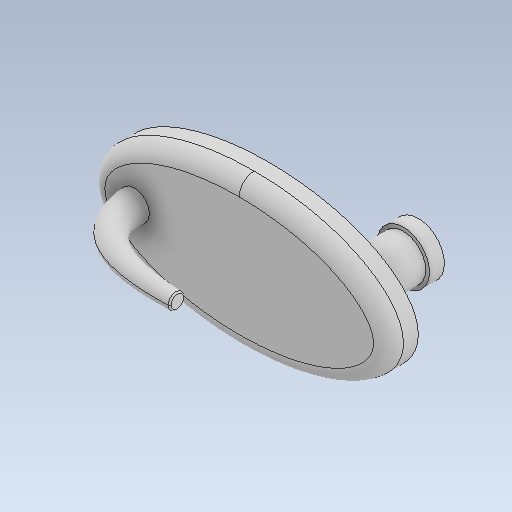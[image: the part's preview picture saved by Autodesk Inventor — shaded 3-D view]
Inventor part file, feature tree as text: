
AUTODESK INVENTOR PART (.ipt)
format: ipt  version: 2020.3 (Build 243373000, 373)  size: 243,200 bytes
history: native  units: in
note: dims shown in document units (in); Inventor stores cm internally (conversion verified against a paired STEP export)
features: other x4, sketch x4
ambient origin geometry x8: Origin, YZ Plane, XZ Plane, XY Plane, X Axis, Y Axis, Z Axis, Center Point
bodies: Solid1 (feature_tree), Solid2 (feature_tree)
feature tree (8):
  other  "hook.ipt"
  other  "Solid1::hook.ipt"
  other  "Solid2::hook.ipt"
  other  "TaggingFeature1"
  sketch  "Sketch1"  dims[d0=0.3937in]
  sketch  "Sketch2"
  sketch  "Sketch3"
  sketch  "Sketch4"
